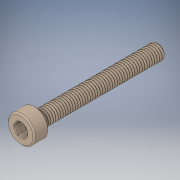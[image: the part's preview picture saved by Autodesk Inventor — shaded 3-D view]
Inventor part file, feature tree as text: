
AUTODESK INVENTOR PART (.ipt)
format: ipt  version: 2019 (Build 230136000, 136)  size: 569,856 bytes
history: mixed  units: mm
features: chamfer x1, imported_body x1
ambient origin geometry x8: Origin, YZ Plane, XZ Plane, XY Plane, X Axis, Y Axis, Z Axis, Center Point
bodies: Solid1 (imported_parasolid)
feature tree (2):
  chamfer  "Chamfer1"  [1 undecoded]
  imported_body  NMx_Import_Brep_tag  [imported B-rep: ~3 faces, bbox_mm=None]
note: 1 required parameter value undecoded (feature->parameter linkage not recoverable at this tier; creation-order binding heuristic only, values carry confidence <= 0.55)
